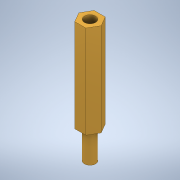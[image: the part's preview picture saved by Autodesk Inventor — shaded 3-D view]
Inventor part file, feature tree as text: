
AUTODESK INVENTOR PART (.ipt)
format: ipt  version: 2022 (Build 260153000, 153)  size: 111,616 bytes
history: native  units: mm
features: sketch x4, extrude x3
ambient origin geometry x8: Origin, YZ Plane, XZ Plane, XY Plane, X Axis, Y Axis, Z Axis, Center Point
bodies: Solid1 (feature_tree)
feature tree (7):
  sketch  "Sketch1"  dims[d0=6.0mm d1=25.0mm d2=0.0mm]
  sketch  "Sketch2"  dims[d3=3.0mm d4=3.0mm]
  extrude  "Extrusion1"  Depth=25.0mm TaperAngle=0.0deg
  sketch  "Sketch3"  dims[d5=8.0mm d6=0.0mm d7=10.0mm d8=0.0mm]
  sketch  "Sketch4"
  extrude  "Extrusion2"  Depth=3.0mm
  extrude  "Extrusion3"  Depth=10.0mm TaperAngle=0.0deg
